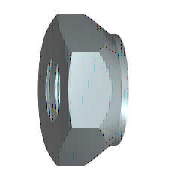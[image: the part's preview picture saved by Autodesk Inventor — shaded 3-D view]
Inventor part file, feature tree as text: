
AUTODESK INVENTOR PART (.ipt)
format: ipt  version: 2018 (Build 220112000, 112)  size: 185,344 bytes
history: native  units: mm (DEFAULTED — no unit token found)
features: sketch x3, hole x1, chamfer x1, other x1, plane x1
ambient origin geometry x7: Origin, YZ Plane, XZ Plane, X Axis, Y Axis, Z Axis, Center Point
bodies: Solid1 (feature_tree), Body (feature_tree)
feature tree (7):
  hole  "Thread"  [1 undecoded]
  chamfer  "Chamfer3"  Distance=5.5mm
  other  "Work Axis1"
  plane  "Work Plane1"
  sketch  "Sketch1"  dims[d0=6.350853mm d1=3.1mm]
  sketch  "Sketch3"  dims[d3=30.0deg d5=5.5mm d6=4.675mm d7=90.0deg d8=8.726646mm d9=1.4mm d24=2.459mm d25=6.0mm d26=4.0mm d27=2.0mm d28=14.3117mm d29=8.0mm d30=20.594885mm d10=0.270633mm d11=30.0deg d12=0.270633mm d13=30.0deg d14=0.0mm d38=0.0mm d39=0.270633mm d40=0.270633mm d41=0.0mm d42=0.0mm]
  sketch  "Sketch2"  dims[d2=0.0mm]
note: 1 required parameter value undecoded (feature->parameter linkage not recoverable at this tier; creation-order binding heuristic only, values carry confidence <= 0.55)
